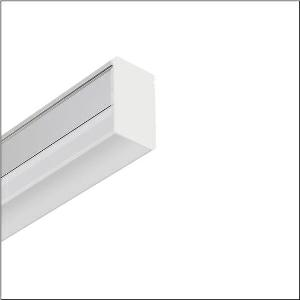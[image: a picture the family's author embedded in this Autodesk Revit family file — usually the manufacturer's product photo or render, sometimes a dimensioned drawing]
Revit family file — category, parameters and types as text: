
# Revit family: batten_41-f_51lp327dm10af
name_source: partatom
category: Lighting Fixtures
units: mm (PartAtom-declared; Revit-internal decimal feet)

## family parameters
Cut with Voids When Loaded = No
Host = Face
Light Source = No
Part Type = Normal
Room Calculation Point = No
Round Connector Dimension = Use Diameter
Shared = No

## types (1)
- --- (1 x LED, 1000 lm, 8.3 W, 5000K)
    Apparent Load = 8 VA
    CIE Flux Codes = 39 68 88 89 100
    Color Rendering = 80
    Color Temperature = 5000K
    Default Elevation = 1800 mm
    Description = Batten 41-F, batten luminaire, primary optical cover: cover, of PC, frosted, light emission: direct distribution, primary light characteristic: symmetric, installation type: surface-mounted, LED, rated luminous flux: 1.000lm, luminous efficacy: 120lm/W, light colour: 830/840/850, colour temperature: 3000/4000/5000K, control gear: ECG, with terminal, 2-pole, mains connection: 220..240V, AC, 50/60Hz, rated input power: 8.3W, housing, of aluminium, silver, length: 580mm, width: 25mm, height: 44mm, end cap, of PC, white, protection rating (complete): IP20, insulation class (complete): insulation class II (safety insulation), certification: CE, permissible operating ambient temperature: -20..+40°C, packaging unit: 1 piece
    Height = 44 mm
    Lamp = 1 x LED
    Lamp Light Flux = 1000 lm
    Lamp Power = 8.3 W
    Lamp count = 1
    Length = 580 mm
    Luminous efficacy = 120 lm/W
    Manufacturer = Siteco
    ModVariant = No
    Model = 51LP327DM10AF
    Mounting Place = Ceiling
    Mounting Type = Surface mounted
    Number of Poles = 1
    OnlyDefault = Yes
    Power Factor = 1
    Product Name = Batten 41-F
    Product group = batten luminaire
    ProductGroupID = 301
    Protection Class = Protection class II
    Protection Degree = IP 20
    RLX_Detail_Level = 1
    RLX_Emergency_Light_Flux = 0 lm
    RLX_Emergency_Type = 0
    RLX_Emergency_Type_DB = No
    RlxData = <blob elided: 27937 chars, md5=95aeda3d>
    Socket = socket
    Standby Power = 0 W
    System Light Flux = 1000 lm
    System Power = 8 W
    Type Comments = individual setting: colour temperature 5000K
    Type Image = l_1007255.jpg
    URL = http://relux.com
    VarID = @adj_000317
    Voltage = 0 V
    Weight = 0.00 kg
    Width = 25 mm  [stored 0.082021 ft]

note: [stored X ft] marks values corroborated as IEEE doubles in the binary element streams (Revit-internal decimal feet)

## geometry (parser evidence)
native form markers: Blend x4, Sweep x13
no freeform markers — native parametric forms only
